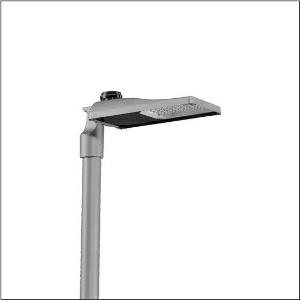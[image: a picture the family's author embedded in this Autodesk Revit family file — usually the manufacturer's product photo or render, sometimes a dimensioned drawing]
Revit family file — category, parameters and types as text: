
# Revit family: streetlight_sl_31_mini___st1_0a_5xh6d35n08ja_1cc2
name_source: partatom
category: Lighting Fixtures
units: mm (PartAtom-declared; Revit-internal decimal feet)

## family parameters
Cut with Voids When Loaded = No
Host = Face
Light Source = No
Part Type = Normal
Room Calculation Point = No
Round Connector Dimension = Use Diameter
Shared = No

## types (1)
- --- (1 x LED, 12140 lm, 81.1 W, 3000K)
    Apparent Load = 81 VA
    CIE Flux Codes = 40 73 97 100 100
    Color Rendering = 70
    Color Temperature = 3000K
    Default Elevation = 1800 mm
    Description = Streetlight SL 31 mini NEMA (7pin), Desk-Remote mast luminaire for post-top, side-entry; light control with lens of PMMA; light distribution: ST1.0a, direct asymmetric distribution, for standard-compliant lighting for roads and squares; LED: luminous flux: 12.140lm, light colour: 730, colour temperature: 3000K; luminous efficacy: 149,7lm/W; control: pre-setting: linear dimming characteristic, flexible luminous flux parameterisation, time-dependent luminous flux control, constant luminous flux control, intelligent temperature release in ECG and LED module, overheat protection; luminaire housing, of diecast aluminium, Siteco® metallic grey (DB 702S), corrosivity category C5 high according to DIN EN ISO 12944; cover of toughened safety glass, transparent, opened without tools; mast flange of diecast aluminium, Siteco® metallic grey (DB 702S), spigot size: 76/60mm, mast flange included unmounted; with cable H07RN-F 3x 1.5mm², cable length: 10,5m, connection cable pre-assembled; mains connection: 220..240V, AC, 50/60Hz; power consumption (at start of service life): 81,1W / (at end of service life): 88,3W / (with reduced operation 50%): 36,4W; protection rating (complete): IP66; insulation class (complete): insulation class I (protective earthing); impact resistance: IK10; certification: CE, ENEC, ENEC+, VDE, UKCA; permissible operating ambient temperature for outdoor applications: -40..+50°C; packaging unit: 1 piece

Light Distribution: ST1.0a
    Height = 76 mm
    Lamp = 1 x LED
    Lamp Light Flux = 12140 lm
    Lamp Power = 81.1 W
    Lamp count = 1
    Length = 547 mm
    Luminous efficacy = 150 lm/W
    Manufacturer = Siteco
    ModVariant = No
    Model = 5XH6D35N08JA
    Number of Poles = 1
    OnlyDefault = Yes
    Power Factor = 1
    Product Name = Streetlight SL 31 mini | ST1.0a
    Product group = mast luminaire | pylon top
    ProductGroupID = 6100
    Protection Class = Protection class I
    Protection Degree = IP 66
    RLX_Detail_Level = 1
    RLX_Emergency_Light_Flux = 0 lm
    RLX_Emergency_Type = 0
    RLX_Emergency_Type_DB = No
    RlxData = <blob elided: 40357 chars, md5=b6365508>
    Socket = socket
    Standby Power = 0 W
    System Light Flux = 12140 lm
    System Power = 81 W
    Type Comments = factory setting: luminous flux: 100 % | dim-lin: 254 | 860 mA
    Type Image = l_1300322.jpg
    URL = http://relux.com
    VarID = @adj_070677
    Voltage = 0 V
    Weight = 0.00 kg
    Width = 265 mm

## geometry (parser evidence)
native form markers: Blend x4, Sweep x11
no freeform markers — native parametric forms only
